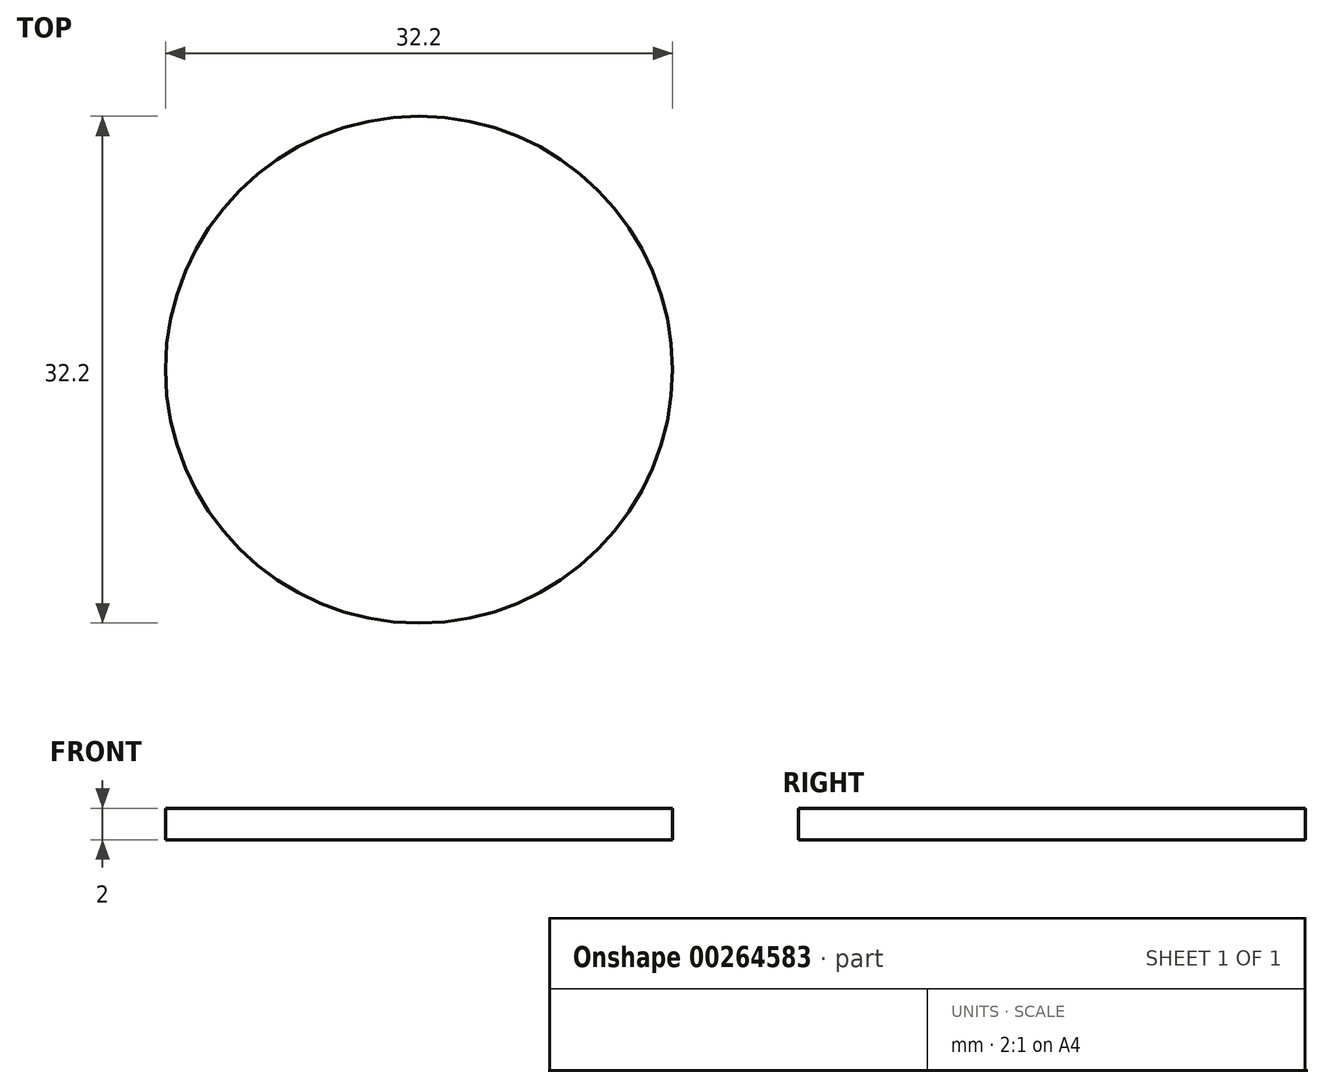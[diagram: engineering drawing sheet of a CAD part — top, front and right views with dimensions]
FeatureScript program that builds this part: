
annotation { "Feature Type Name" : "Feature", "Feature Type Description" : "" }
export const myFeature = defineFeature(function(context is Context, id is Id, definition is map)
    precondition{}
    {
        {
            var Q0;
            Q0=qCreatedBy(makeId("Top.planeOp"),FACE);
            var sketch = newSketch(context, id + "F0", { "sketchPlane" : qUnion([Q0])});
            skCircle(sketch, "E0", {"center": v(0, 0) * mm, "radius": 16.1 * mm});
            skSolve(sketch);
        }
        {
            var Q0;
            Q0 = qSketchRegion(id + "F0", true);
            extrude(context, id + "F1", {"entities" : qUnion([Q0]), "depth" : 2 * mm});
        }
    });
